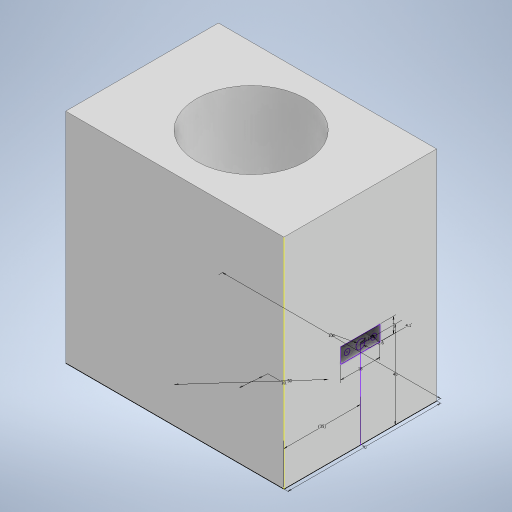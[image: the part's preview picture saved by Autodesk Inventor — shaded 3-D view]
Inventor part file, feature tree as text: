
AUTODESK INVENTOR PART (.ipt)
format: ipt  version: 2024 (Build 280153000, 153)  size: 223,744 bytes
history: native  units: mm
features: extrude x4, sketch x2, hole x2, other x1
ambient origin geometry x8: Origin, YZ Plane, XZ Plane, XY Plane, X Axis, Y Axis, Z Axis, Center Point
bodies: Body1 (feature_tree)
feature tree (9):
  other  "實體1"
  sketch  "草圖1"
  extrude  "擠出1"  Depth=100.0mm
  extrude  "擠出2"  Depth=70.0mm
  extrude  "擠出3"  Depth=50.0mm
  sketch  "草圖2"
  hole  "孔1"  [1 undecoded]
  extrude  "擠出4"  Depth=15.0mm TaperAngle=0.0deg
  hole  "孔2"  [1 undecoded]
note: 2 required parameter values undecoded (feature->parameter linkage not recoverable at this tier; creation-order binding heuristic only, values carry confidence <= 0.55)
